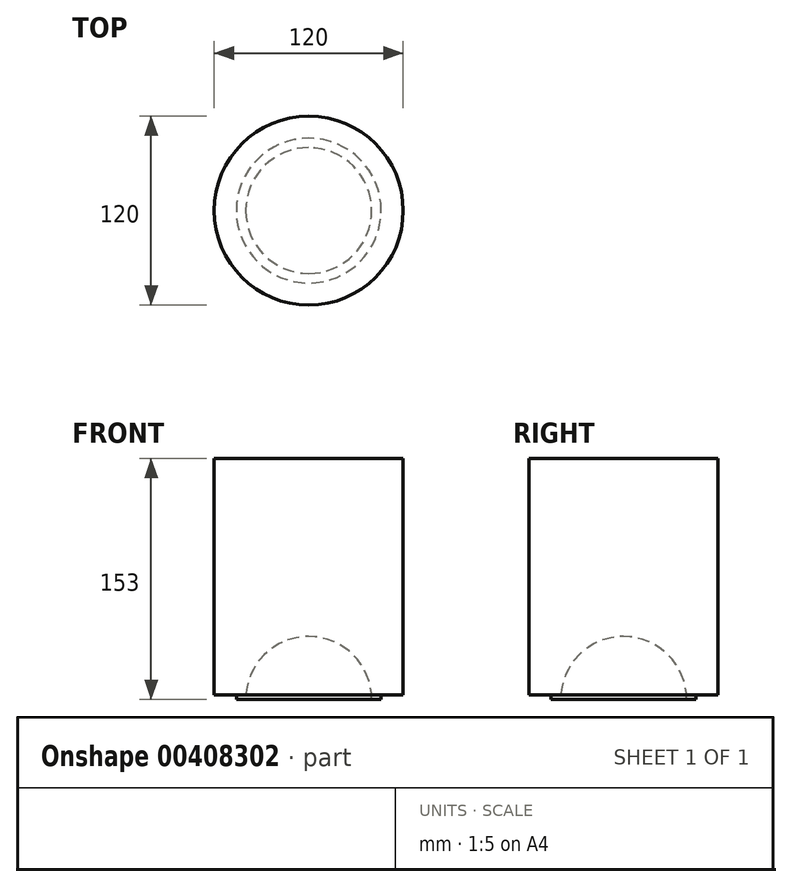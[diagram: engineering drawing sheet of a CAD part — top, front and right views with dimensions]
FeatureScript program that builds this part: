
annotation { "Feature Type Name" : "Feature", "Feature Type Description" : "" }
export const myFeature = defineFeature(function(context is Context, id is Id, definition is map)
    precondition{}
    {
        {
            var Q0;
            Q0=qCreatedBy(makeId("Top.planeOp"),FACE);
            var sketch = newSketch(context, id + "F0", { "sketchPlane" : qUnion([Q0])});
            skCircle(sketch, "E0", {"center": v(0, 0) * mm, "radius": 60 * mm});
            skSolve(sketch);
        }
        {
            var Q0;
            Q0=makeQuery(id+"F0.imprint","IMPRINT",FACE,{"disambiguationData":[TD([[makeQuery(id+"F0.imprint","IMPRINT",EDGE,{"derivedFrom":sQuery(id+"F0.wireOp",EDGE,"E0")}),1.0]])]});
            var Q1;
            Q1=makeQuery(id+"F0.imprint","IMPRINT",FACE,{"disambiguationData":[TD([[makeQuery(id+"F0.imprint","IMPRINT",EDGE,{"derivedFrom":sQuery(id+"F0.wireOp",EDGE,"eopkjbcp-2Ti5-YKfy-ORrA-FJhuTVvvbj5o")}),1.0]])]});
            extrude(context, id + "F1", {"entities" : qUnion([Q0, Q1]), "depth" : 150 * mm});
        }
        {
            var Q0;
            Q0=makeQuery(id+"F1.opExtrude","CAP_FACE",FACE,{"disambiguationData":[OSD([sQuery(id+"F0.wireOp",EDGE,"E0")])],"isStart":true});
            var sketch = newSketch(context, id + "F2", { "sketchPlane" : qUnion([Q0])});
            skCircle(sketch, "E1", {"center": v(0, 0) * mm, "radius": 46 * mm});
            skSolve(sketch);
        }
        {
            var Q0;
            Q0=makeQuery(id+"F2.imprint","IMPRINT",FACE,{"disambiguationData":[TD([[makeQuery(id+"F2.imprint","IMPRINT",EDGE,{"derivedFrom":sQuery(id+"F2.wireOp",EDGE,"E1")}),1.0]])]});
            extrude(context, id + "F3", {"entities" : qUnion([Q0]), "operationType" : NewBodyOperationType.ADD, "depth" : 3 * mm});
        }
        {
            var Q0;
            Q0=makeQuery(id+"F3.opExtrude","CAP_FACE",FACE,{"disambiguationData":[OSD([sQuery(id+"F2.wireOp",EDGE,"E1")])],"isStart":false});
            var sketch = newSketch(context, id + "F4", { "sketchPlane" : qUnion([Q0])});
            skArc(sketch, "E2", {"start": v(0, -40) * mm, "mid": v(40, 0) * mm, "end": v(0, 40) * mm});
            skLineSegment(sketch, "E3", {"start": v(0, -40) * mm, "end": v(0, 40) * mm});
            skSolve(sketch);
        }
        {
            var Q0;
            Q0=makeQuery(id+"F4.imprint","IMPRINT",FACE,{"disambiguationData":[TD([[makeQuery(id+"F4.imprint","IMPRINT",EDGE,{"derivedFrom":sQuery(id+"F4.wireOp",EDGE,"E2")}),1.0]])]});
            var Q1;
            Q1=sQuery(id+"F4.wireOp",EDGE,"E3");
            revolve(context, id + "F5", {"operationType" : NewBodyOperationType.REMOVE, "entities" : qUnion([Q0]), "axis" : qUnion([Q1]), "revolveType" : RevolveType.FULL, "oppositeDirection" : true});
        }
    });
